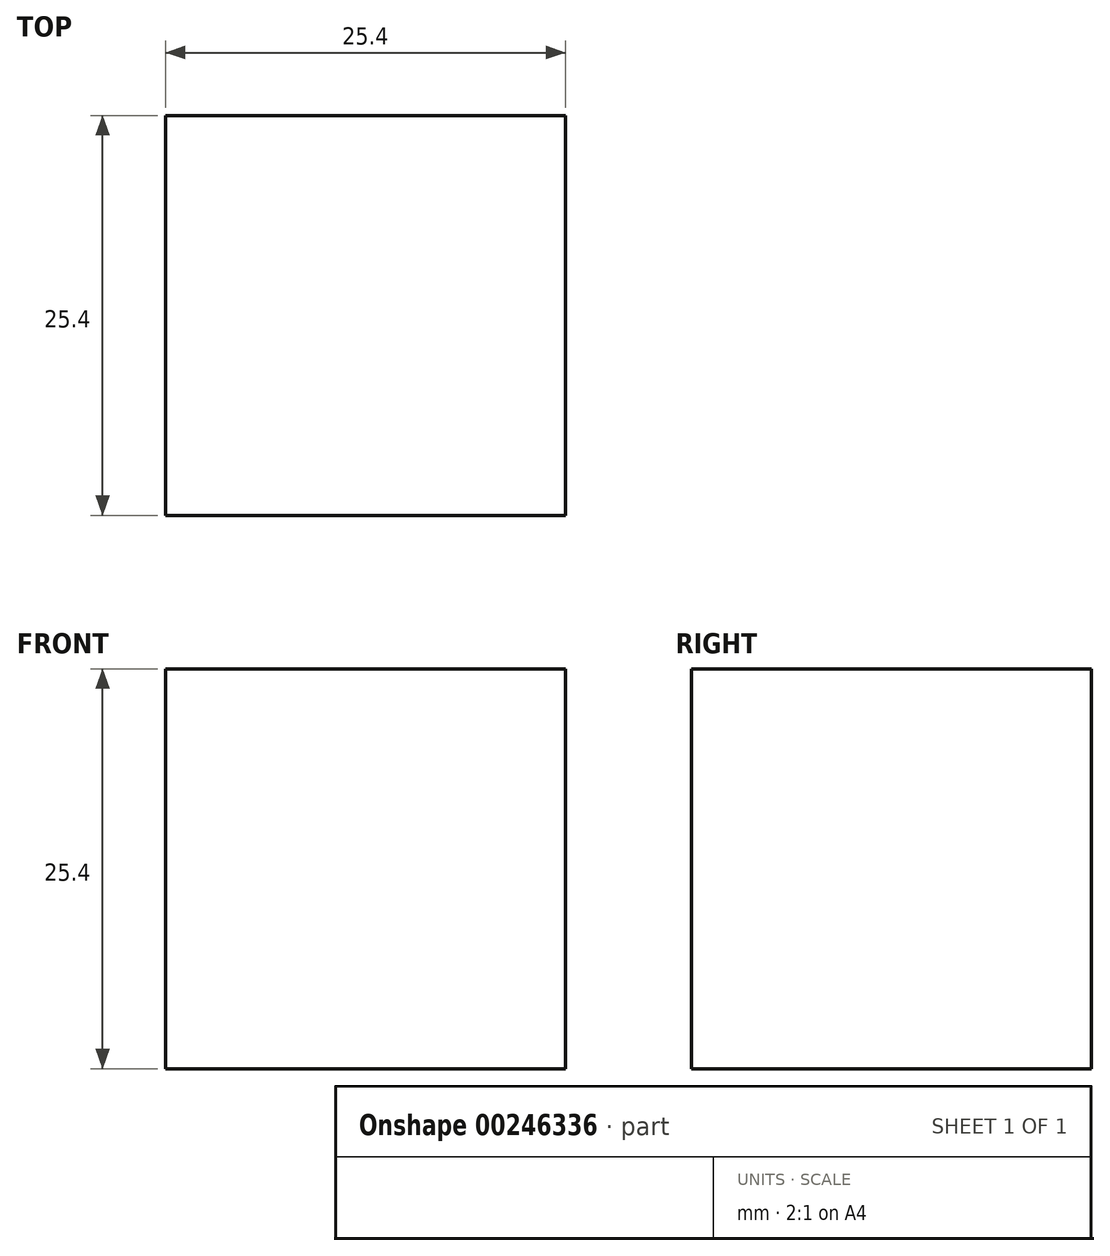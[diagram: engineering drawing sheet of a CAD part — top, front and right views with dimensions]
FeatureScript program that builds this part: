
annotation { "Feature Type Name" : "Feature", "Feature Type Description" : "" }
export const myFeature = defineFeature(function(context is Context, id is Id, definition is map)
    precondition{}
    {
        {
            var Q0;
            Q0=qCreatedBy(makeId("Top.planeOp"),FACE);
            var sketch = newSketch(context, id + "F0", { "sketchPlane" : qUnion([Q0])});
            skLineSegment(sketch, "E0.bottom", {"start": v(-4.9, 35.05) * mm, "end": v(20.5, 35.05) * mm});
            skLineSegment(sketch, "E0.top", {"start": v(-4.9, 9.65) * mm, "end": v(20.5, 9.65) * mm});
            skLineSegment(sketch, "E0.left", {"start": v(-4.9, 35.05) * mm, "end": v(-4.9, 9.65) * mm});
            skLineSegment(sketch, "E0.right", {"start": v(20.5, 35.05) * mm, "end": v(20.5, 9.65) * mm});
            skSolve(sketch);
        }
        {
            var Q0;
            Q0=makeQuery(id+"F0.imprint","IMPRINT",FACE,{"disambiguationData":[TD([[makeQuery(id+"F0.imprint","IMPRINT",EDGE,{"derivedFrom":sQuery(id+"F0.wireOp",EDGE,"E0.bottom")}),-1.0]])]});
            extrude(context, id + "F1", {"entities" : qUnion([Q0]), "depth" : 25.4 * mm});
        }
    });
